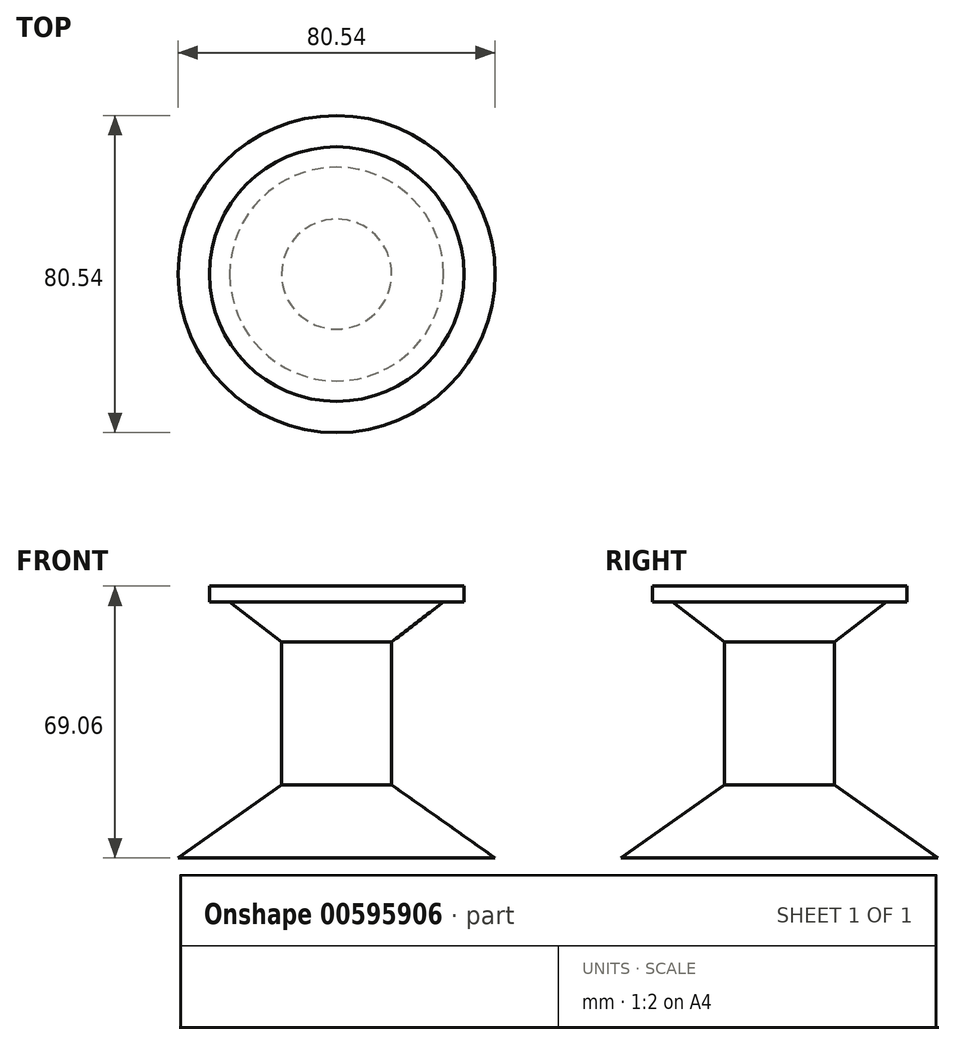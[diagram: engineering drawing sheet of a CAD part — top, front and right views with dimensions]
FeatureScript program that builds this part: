
annotation { "Feature Type Name" : "Feature", "Feature Type Description" : "" }
export const myFeature = defineFeature(function(context is Context, id is Id, definition is map)
    precondition{}
    {
        {
            var Q0;
            Q0=qCreatedBy(makeId("Front.planeOp"),FACE);
            var sketch = newSketch(context, id + "F0", { "sketchPlane" : qUnion([Q0])});
            skLineSegment(sketch, "E0", {"start": v(-40.27, 0) * mm, "end": v(-13.98, 18.57) * mm});
            skLineSegment(sketch, "E1", {"start": v(-13.98, 18.57) * mm, "end": v(-13.98, 54.88) * mm});
            skLineSegment(sketch, "E2", {"start": v(-13.98, 54.88) * mm, "end": v(-32.34, 69.06) * mm});
            skLineSegment(sketch, "E3", {"start": v(-32.34, 69.06) * mm, "end": v(0, 69.06) * mm});
            skLineSegment(sketch, "E4", {"start": v(0, 0) * mm, "end": v(-40.27, 0) * mm});
            skLineSegment(sketch, "E5", {"start": v(0, 69.06) * mm, "end": v(0, 0) * mm});
            skSolve(sketch);
        }
        {
            var Q0;
            Q0 = qSketchRegion(id + "F0", true);
            var Q1;
            Q1=sQuery(id+"F0.wireOp",EDGE,"E5");
            revolve(context, id + "F1", {"entities" : qUnion([Q0]), "axis" : qUnion([Q1]), "revolveType" : RevolveType.FULL});
        }
        {
            var Q0;
            Q0=makeQuery(id+"F1.opRevolve","SWEPT_FACE",FACE,{"disambiguationData":[OSD([sQuery(id+"F0.wireOp",EDGE,"E3")])]});
            extrude(context, id + "F2", {"entities" : qUnion([Q0]), "operationType" : NewBodyOperationType.ADD, "oppositeDirection" : true, "depth" : 4 * mm, "offsetDistance" : 25 * mm});
        }
    });
